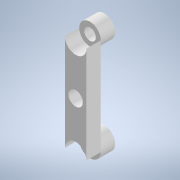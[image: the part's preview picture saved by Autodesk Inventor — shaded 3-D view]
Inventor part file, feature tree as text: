
AUTODESK INVENTOR PART (.ipt)
format: ipt  version: 2022 (Build 260153000, 153)  size: 139,776 bytes
history: native  units: mm
features: reference x8, other x3, extrude x2, sketch x2, fillet x1
ambient origin geometry x8: Origin, YZ Plane, XZ Plane, XY Plane, X Axis, Y Axis, Z Axis, Center Point
bodies: Solid1 (feature_tree)
feature tree (16):
  extrude  "Extrusion1"  Depth=10.0mm
  extrude  "Extrusion2"  Depth=2.0mm
  fillet  "Fillet1"  [1 undecoded]
  sketch  "Sketch1"  dims[d0=10.0mm d1=0.0mm d2=10.0mm]
  reference  "Reference1"
  reference  "Reference2"
  reference  "Reference3"
  reference  "Reference4"
  reference  "Reference5"
  reference  "Reference6"
  sketch  "Sketch2"  dims[d3=10.0mm d4=0.0mm d5=2.0mm]
  reference  "Reference7"
  reference  "Reference8"
  other  "<userpath>\OneDrive\Namizje\school\3. letnik\ZOPp\laserski merilnik\3d model\Assembly1.iam"
  other  "Assembly1.iam"
  other  "Hold of motors:1"
note: 1 required parameter value undecoded (feature->parameter linkage not recoverable at this tier; creation-order binding heuristic only, values carry confidence <= 0.55)
